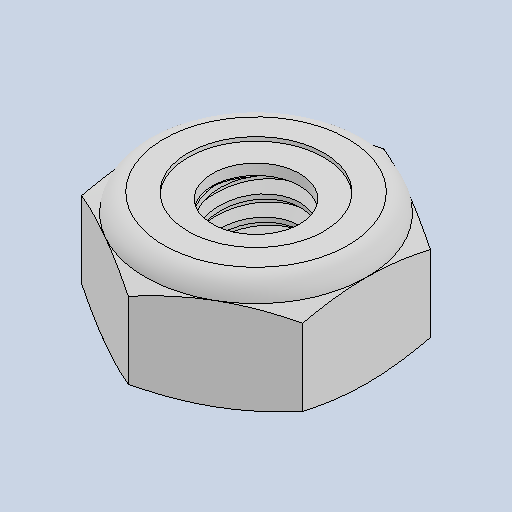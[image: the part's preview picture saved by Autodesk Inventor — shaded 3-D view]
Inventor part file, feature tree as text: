
AUTODESK INVENTOR PART (.ipt)
format: ipt  version: 2022 (Build 260153000, 153)  size: 271,360 bytes
history: native  units: in
note: dims shown in document units (in); Inventor stores cm internally (conversion verified against a paired STEP export)
features: other x1, revolve x1
ambient origin geometry x8: Origin, YZ Plane, XZ Plane, XY Plane, X Axis, Y Axis, Z Axis, Center Point
bodies: Solid1 (feature_tree), Solid2 (feature_tree)
feature tree (2):
  other  "Cut-Revolve4"
  revolve  "Revolve2"  [1 undecoded]
note: 1 required parameter value undecoded (feature->parameter linkage not recoverable at this tier; creation-order binding heuristic only, values carry confidence <= 0.55)
